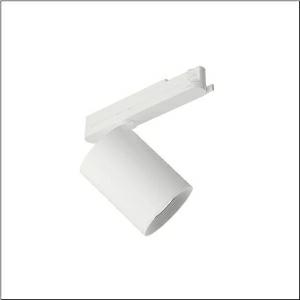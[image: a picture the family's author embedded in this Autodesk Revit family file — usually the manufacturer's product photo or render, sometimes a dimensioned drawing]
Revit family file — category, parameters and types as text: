
# Revit family: spot_11_51sd15mbb5a
name_source: partatom
category: Lighting Fixtures
units: mm (PartAtom-declared; Revit-internal decimal feet)

## family parameters
Cut with Voids When Loaded = No
Host = Face
Light Source = No
Part Type = Normal
Room Calculation Point = No
Round Connector Dimension = Use Diameter
Shared = No

## types (1)
- --- (1 x LED, 7370 lm, 50.2 W, 3000K)
    Apparent Load = 50 VA
    CIE Flux Codes = 91 98 100 100 100
    Color Rendering = 90
    Color Temperature = 3000K
    Default Elevation = 1800 mm
    Description = Spot 11, directional spotlight, light control with lens, of PMMA, LED rated luminous flux: 5.750lm, light colour: 930, control gear: ECG Multilumen, with 3-phase adapter, mains connection: 220..240V, AC, 50/60Hz, of aluminium, traffic white (RAL 9016), length: 213mm, diameter: 105mm, protection rating (complete): IP20, insulation class (complete): insulation class I (protective earthing), certification: CE, impact resistance: IK02, permissible ambient temperature for indoor applications: -20..+40°C, packaging unit: 1 piece
    Height = 175 mm
    Lamp = 1 x LED
    Lamp Light Flux = 7370 lm
    Lamp Power = 50.2 W
    Lamp count = 1
    Length = 105 mm
    Luminous efficacy = 147 lm/W
    Manufacturer = Siteco
    ModVariant = No
    Model = 51SD15MBB5A
    Mounting Place = Ceiling
    Mounting Type = Pendant
    Number of Poles = 1
    OnlyDefault = Yes
    Power Factor = 1
    Product Name = Spot 11
    Product group = directional spotlight
    ProductGroupID = 906
    Protection Class = Protection class I
    Protection Degree = IP 20
    RLX_Detail_Level = 1
    RLX_Emergency_Light_Flux = 0 lm
    RLX_Emergency_Type = 0
    RLX_Emergency_Type_DB = No
    RlxData = <blob elided: 17729 chars, md5=9451cdc2>
    Socket = socket
    Standby Power = 0 W
    System Light Flux = 7370 lm
    System Power = 50 W
    Type Comments = factory setting: luminous flux: 100 % | (ON | ON | ON | ON) | 1050 mA
    Type Image = l_1006697.jpg
    URL = http://relux.com
    VarID = @adj_146970
    Voltage = 0 V
    Weight = 0.00 kg
    Width = 0 mm  [stored 0 ft]

note: [stored X ft] marks values corroborated as IEEE doubles in the binary element streams (Revit-internal decimal feet)

## geometry (parser evidence)
native form markers: Blend x4, Sweep x10
no freeform markers — native parametric forms only
